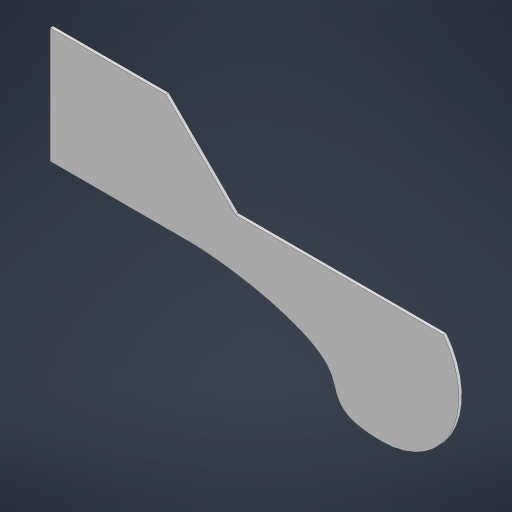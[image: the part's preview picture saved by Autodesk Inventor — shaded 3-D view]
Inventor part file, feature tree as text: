
AUTODESK INVENTOR PART (.ipt)
format: ipt  version: 2024 (Build 280153000, 153)  size: 180,224 bytes
history: native  units: in
note: dims shown in document units (in); Inventor stores cm internally (conversion verified against a paired STEP export)
features: extrude x1, sketch x1
ambient origin geometry x8: Origin, YZ Plane, XZ Plane, XY Plane, X Axis, Y Axis, Z Axis, Center Point
bodies: Solid1 (feature_tree)
feature tree (2):
  extrude  "Extrusion1"  [1 undecoded]
  sketch  "Sketch1"  dims[d0=0.0625in d1=0.0in]
note: 1 required parameter value undecoded (feature->parameter linkage not recoverable at this tier; creation-order binding heuristic only, values carry confidence <= 0.55)
